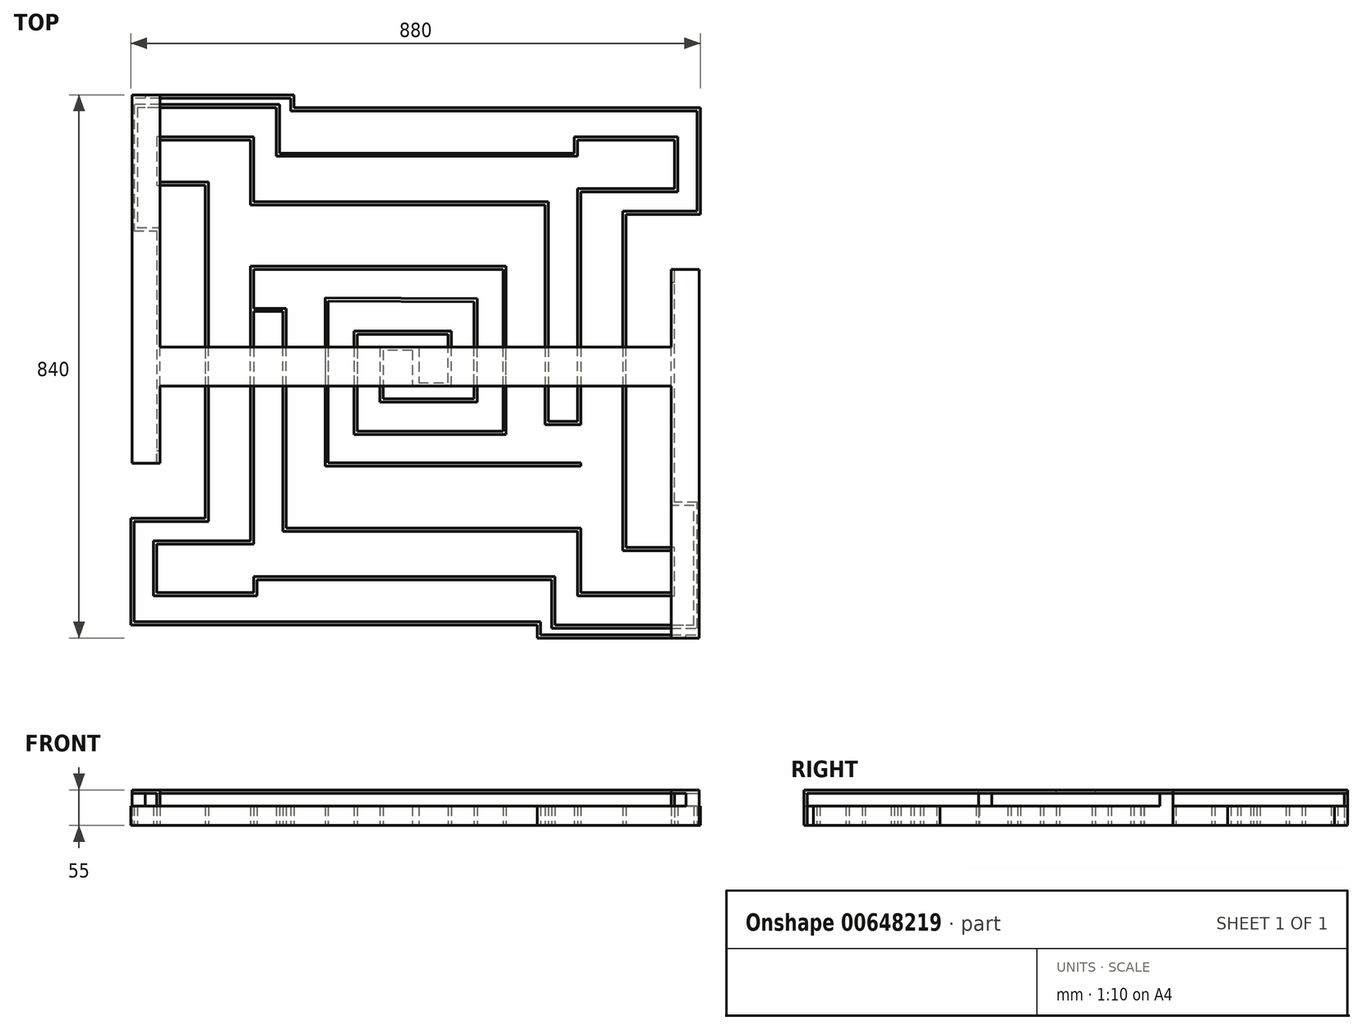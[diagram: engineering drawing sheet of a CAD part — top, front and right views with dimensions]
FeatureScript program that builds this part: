
annotation { "Feature Type Name" : "Feature", "Feature Type Description" : "" }
export const myFeature = defineFeature(function(context is Context, id is Id, definition is map)
    precondition{}
    {
        {
            var Q0;
            Q0=qCreatedBy(makeId("Top.planeOp"),FACE);
            var sketch = newSketch(context, id + "F0", { "sketchPlane" : qUnion([Q0])});
            skLineSegment(sketch, "E0.bottom", {"start": v(150, 150) * mm, "end": v(-150, 150) * mm, "construction": true});
            skLineSegment(sketch, "E0.top", {"start": v(150, -150) * mm, "end": v(-150, -150) * mm, "construction": true});
            skLineSegment(sketch, "E0.left", {"start": v(150, 150) * mm, "end": v(150, -150) * mm, "construction": true});
            skLineSegment(sketch, "E0.right", {"start": v(-150, 150) * mm, "end": v(-150, -150) * mm, "construction": true});
            skPoint(sketch, "E0.middle", {"position": v(0, 0) * mm});
            skPoint(sketch, "E1.0.1.0", {"position": v(0, 325) * mm});
            skLineSegment(sketch, "E1.0.1.1", {"start": v(-150, 475) * mm, "end": v(-150, 175) * mm, "construction": true});
            skLineSegment(sketch, "E1.0.1.2", {"start": v(150, 475) * mm, "end": v(150, 175) * mm, "construction": true});
            skLineSegment(sketch, "E1.0.1.3", {"start": v(150, 175) * mm, "end": v(-150, 175) * mm, "construction": true});
            skLineSegment(sketch, "E1.0.1.4", {"start": v(150, 475) * mm, "end": v(-150, 475) * mm, "construction": true});
            skLineSegment(sketch, "E1.0.2.1", {"start": v(-150, 800) * mm, "end": v(-150, 500) * mm, "construction": true});
            skLineSegment(sketch, "E1.0.2.2", {"start": v(150, 800) * mm, "end": v(150, 500) * mm, "construction": true});
            skLineSegment(sketch, "E1.0.2.3", {"start": v(150, 500) * mm, "end": v(-150, 500) * mm, "construction": true});
            skLineSegment(sketch, "E1.0.2.4", {"start": v(150, 800) * mm, "end": v(-150, 800) * mm, "construction": true});
            skPoint(sketch, "E1.1.0.0", {"position": v(325, 0) * mm});
            skLineSegment(sketch, "E1.1.0.1", {"start": v(175, 150) * mm, "end": v(175, -150) * mm, "construction": true});
            skLineSegment(sketch, "E1.1.0.2", {"start": v(475, 150) * mm, "end": v(475, -150) * mm, "construction": true});
            skLineSegment(sketch, "E1.1.0.3", {"start": v(475, -150) * mm, "end": v(175, -150) * mm, "construction": true});
            skLineSegment(sketch, "E1.1.0.4", {"start": v(475, 150) * mm, "end": v(175, 150) * mm, "construction": true});
            skPoint(sketch, "E1.1.1.0", {"position": v(325, 325) * mm});
            skLineSegment(sketch, "E1.1.1.1", {"start": v(175, 475) * mm, "end": v(175, 175) * mm, "construction": true});
            skLineSegment(sketch, "E1.1.1.2", {"start": v(475, 475) * mm, "end": v(475, 175) * mm, "construction": true});
            skLineSegment(sketch, "E1.1.1.3", {"start": v(475, 175) * mm, "end": v(175, 175) * mm, "construction": true});
            skLineSegment(sketch, "E1.1.1.4", {"start": v(475, 475) * mm, "end": v(175, 475) * mm, "construction": true});
            skPoint(sketch, "E1.1.2.0", {"position": v(325, 650) * mm});
            skLineSegment(sketch, "E1.1.2.1", {"start": v(175, 800) * mm, "end": v(175, 500) * mm, "construction": true});
            skLineSegment(sketch, "E1.1.2.2", {"start": v(475, 800) * mm, "end": v(475, 500) * mm, "construction": true});
            skLineSegment(sketch, "E1.1.2.3", {"start": v(475, 500) * mm, "end": v(175, 500) * mm, "construction": true});
            skLineSegment(sketch, "E1.1.2.4", {"start": v(475, 800) * mm, "end": v(175, 800) * mm, "construction": true});
            skLineSegment(sketch, "E1.2.0.1", {"start": v(500, 150) * mm, "end": v(500, -150) * mm, "construction": true});
            skLineSegment(sketch, "E1.2.0.2", {"start": v(800, 150) * mm, "end": v(800, -150) * mm, "construction": true});
            skLineSegment(sketch, "E1.2.0.3", {"start": v(800, -150) * mm, "end": v(500, -150) * mm, "construction": true});
            skLineSegment(sketch, "E1.2.0.4", {"start": v(800, 150) * mm, "end": v(500, 150) * mm, "construction": true});
            skPoint(sketch, "E1.2.1.0", {"position": v(650, 325) * mm});
            skLineSegment(sketch, "E1.2.1.1", {"start": v(500, 475) * mm, "end": v(500, 175) * mm, "construction": true});
            skLineSegment(sketch, "E1.2.1.2", {"start": v(800, 475) * mm, "end": v(800, 175) * mm, "construction": true});
            skLineSegment(sketch, "E1.2.1.3", {"start": v(800, 175) * mm, "end": v(500, 175) * mm, "construction": true});
            skLineSegment(sketch, "E1.2.1.4", {"start": v(800, 475) * mm, "end": v(500, 475) * mm, "construction": true});
            skLineSegment(sketch, "E1.2.2.1", {"start": v(500, 800) * mm, "end": v(500, 500) * mm, "construction": true});
            skLineSegment(sketch, "E1.2.2.2", {"start": v(800, 800) * mm, "end": v(800, 500) * mm, "construction": true});
            skLineSegment(sketch, "E1.2.2.3", {"start": v(800, 500) * mm, "end": v(500, 500) * mm, "construction": true});
            skLineSegment(sketch, "E1.2.2.4", {"start": v(800, 800) * mm, "end": v(500, 800) * mm, "construction": true});
            skLineSegment(sketch, "E1.direction1", {"start": v(-150, -150) * mm, "end": v(175, -150) * mm, "construction": true});
            skLineSegment(sketch, "E1.direction2", {"start": v(-150, -150) * mm, "end": v(-150, 175) * mm, "construction": true});
            skLineSegment(sketch, "E2", {"start": v(190, 425.96) * mm, "end": v(190, 175.96) * mm});
            skLineSegment(sketch, "E3", {"start": v(190, 175.96) * mm, "end": v(580, 175.96) * mm});
            skLineSegment(sketch, "E4", {"start": v(325, 350) * mm, "end": v(275, 350) * mm});
            skLineSegment(sketch, "E5", {"start": v(275, 350) * mm, "end": v(275, 275) * mm});
            skLineSegment(sketch, "E6", {"start": v(415, 275) * mm, "end": v(415, 425) * mm});
            skLineSegment(sketch, "E7", {"start": v(275, 275) * mm, "end": v(415, 275) * mm});
            skLineSegment(sketch, "E8", {"start": v(415, 425) * mm, "end": v(190, 425.96) * mm});
            skLineSegment(sketch, "E9", {"start": v(325, 350) * mm, "end": v(325, 300) * mm, "construction": true});
            skLineSegment(sketch, "E10", {"start": v(325, 300) * mm, "end": v(375, 300) * mm});
            skLineSegment(sketch, "E11", {"start": v(375, 300) * mm, "end": v(375, 375) * mm});
            skLineSegment(sketch, "E12", {"start": v(375, 375) * mm, "end": v(235, 375) * mm});
            skLineSegment(sketch, "E13", {"start": v(235, 375) * mm, "end": v(235, 225) * mm});
            skLineSegment(sketch, "E14", {"start": v(235, 225) * mm, "end": v(460, 225) * mm});
            skLineSegment(sketch, "E15", {"start": v(460, 225) * mm, "end": v(460, 475) * mm});
            skLineSegment(sketch, "E16", {"start": v(460, 475) * mm, "end": v(70, 475) * mm});
            skLineSegment(sketch, "E17.0", {"start": v(465, 480) * mm, "end": v(70, 480) * mm});
            skLineSegment(sketch, "E17.1", {"start": v(465, 220) * mm, "end": v(465, 480) * mm});
            skLineSegment(sketch, "E17.2", {"start": v(230, 220) * mm, "end": v(465, 220) * mm});
            skLineSegment(sketch, "E17.3", {"start": v(325, 295) * mm, "end": v(380, 295) * mm});
            skLineSegment(sketch, "E17.4", {"start": v(380, 295) * mm, "end": v(380, 380) * mm});
            skLineSegment(sketch, "E17.5", {"start": v(380, 380) * mm, "end": v(230, 380) * mm});
            skLineSegment(sketch, "E17.6", {"start": v(230, 380) * mm, "end": v(230, 220) * mm});
            skLineSegment(sketch, "E18", {"start": v(70, 480) * mm, "end": v(70, 475) * mm});
            skLineSegment(sketch, "E19", {"start": v(325, 300) * mm, "end": v(325, 295) * mm});
            skLineSegment(sketch, "E20.0", {"start": v(185, 170.96) * mm, "end": v(580, 170.96) * mm});
            skLineSegment(sketch, "E20.1", {"start": v(185, 430.98) * mm, "end": v(185, 170.96) * mm});
            skLineSegment(sketch, "E20.2", {"start": v(420, 429.98) * mm, "end": v(185, 430.98) * mm});
            skLineSegment(sketch, "E20.3", {"start": v(325, 355) * mm, "end": v(270, 355) * mm});
            skLineSegment(sketch, "E20.4", {"start": v(270, 355) * mm, "end": v(270, 270) * mm});
            skLineSegment(sketch, "E20.5", {"start": v(270, 270) * mm, "end": v(420, 270) * mm});
            skLineSegment(sketch, "E20.6", {"start": v(420, 270) * mm, "end": v(420, 429.98) * mm});
            skLineSegment(sketch, "E21", {"start": v(580, 175.96) * mm, "end": v(580, 170.96) * mm});
            skLineSegment(sketch, "E22", {"start": v(325, 355) * mm, "end": v(325, 350) * mm});
            skLineSegment(sketch, "E23", {"start": v(125, 75) * mm, "end": v(125, 150) * mm});
            skLineSegment(sketch, "E24", {"start": v(75, 150) * mm, "end": v(75, 50) * mm});
            skLineSegment(sketch, "E25", {"start": v(75, 50) * mm, "end": v(-75, 50) * mm});
            skLineSegment(sketch, "E26", {"start": v(-75, 50) * mm, "end": v(-75, -25) * mm});
            skLineSegment(sketch, "E27", {"start": v(-75, -25) * mm, "end": v(75, -25) * mm});
            skLineSegment(sketch, "E28", {"start": v(75, -25) * mm, "end": v(75, 0) * mm});
            skLineSegment(sketch, "E29", {"start": v(75, 0) * mm, "end": v(150, 0) * mm});
            skLineSegment(sketch, "E30", {"start": v(175, -75) * mm, "end": v(475, -75) * mm});
            skLineSegment(sketch, "E31", {"start": v(125, 75) * mm, "end": v(150, 75) * mm});
            skLineSegment(sketch, "E32", {"start": v(150, -75) * mm, "end": v(-115, -75) * mm});
            skLineSegment(sketch, "E33", {"start": v(-115, -75) * mm, "end": v(-115, 90) * mm});
            skLineSegment(sketch, "E34", {"start": v(-115, 90) * mm, "end": v(0, 90) * mm});
            skLineSegment(sketch, "E35", {"start": v(0, 90) * mm, "end": v(0, 150) * mm});
            skLineSegment(sketch, "E36", {"start": v(175, 0) * mm, "end": v(475, 0) * mm});
            skLineSegment(sketch, "E37", {"start": v(175, 75) * mm, "end": v(475, 75) * mm});
            skLineSegment(sketch, "E38", {"start": v(325, 150) * mm, "end": v(325, -150) * mm, "construction": true});
            skLineSegment(sketch, "E39.0", {"start": v(120, 70) * mm, "end": v(150, 70) * mm});
            skLineSegment(sketch, "E39.1", {"start": v(120, 70) * mm, "end": v(120, 150) * mm});
            skLineSegment(sketch, "E40.0", {"start": v(80, -5) * mm, "end": v(150, -5) * mm});
            skLineSegment(sketch, "E40.1", {"start": v(80, -30) * mm, "end": v(80, -5) * mm});
            skLineSegment(sketch, "E40.2", {"start": v(70, 150) * mm, "end": v(70, 55) * mm});
            skLineSegment(sketch, "E40.3", {"start": v(70, 55) * mm, "end": v(-80, 55) * mm});
            skLineSegment(sketch, "E40.4", {"start": v(-80, 55) * mm, "end": v(-80, -30) * mm});
            skLineSegment(sketch, "E40.5", {"start": v(-80, -30) * mm, "end": v(80, -30) * mm});
            skLineSegment(sketch, "E41.0", {"start": v(5, 85) * mm, "end": v(5, 150) * mm});
            skLineSegment(sketch, "E41.1", {"start": v(-110, 85) * mm, "end": v(5, 85) * mm});
            skLineSegment(sketch, "E41.2", {"start": v(-110, -70) * mm, "end": v(-110, 85) * mm});
            skLineSegment(sketch, "E41.3", {"start": v(150, -70) * mm, "end": v(-110, -70) * mm});
            skLineSegment(sketch, "E42.0", {"start": v(175, 70) * mm, "end": v(475, 70) * mm});
            skLineSegment(sketch, "E43.0", {"start": v(175, -5) * mm, "end": v(475, -5) * mm});
            skLineSegment(sketch, "E44.0", {"start": v(175, -70) * mm, "end": v(475, -70) * mm});
            skLineSegment(sketch, "E45", {"start": v(0, 175) * mm, "end": v(0, 475) * mm});
            skLineSegment(sketch, "E46", {"start": v(-75, 175) * mm, "end": v(-75, 475) * mm});
            skLineSegment(sketch, "E47", {"start": v(175, 75) * mm, "end": v(150, 75) * mm});
            skLineSegment(sketch, "E48", {"start": v(175, 70) * mm, "end": v(150, 70) * mm});
            skLineSegment(sketch, "E49", {"start": v(175, 0) * mm, "end": v(150, 0) * mm});
            skLineSegment(sketch, "E50", {"start": v(175, -5) * mm, "end": v(150, -5) * mm});
            skLineSegment(sketch, "E51", {"start": v(175, -70) * mm, "end": v(150, -70) * mm});
            skLineSegment(sketch, "E52", {"start": v(175, -75) * mm, "end": v(150, -75) * mm});
            skLineSegment(sketch, "E53.0", {"start": v(5, 175) * mm, "end": v(5, 475) * mm});
            skLineSegment(sketch, "E54", {"start": v(5, 150) * mm, "end": v(5, 175) * mm});
            skLineSegment(sketch, "E55", {"start": v(70, 150) * mm, "end": v(70, 175) * mm});
            skLineSegment(sketch, "E56", {"start": v(75, 150) * mm, "end": v(75, 175) * mm});
            skLineSegment(sketch, "E57", {"start": v(120, 150) * mm, "end": v(120, 175) * mm});
            skLineSegment(sketch, "E58", {"start": v(125, 150) * mm, "end": v(125, 175) * mm});
            skLineSegment(sketch, "E59.MirrorCS", {"start": v(475, -75) * mm, "end": v(500, -75) * mm});
            skLineSegment(sketch, "E60.MirrorCS", {"start": v(475, -70) * mm, "end": v(500, -70) * mm});
            skLineSegment(sketch, "E61.MirrorCS", {"start": v(475, 70) * mm, "end": v(500, 70) * mm});
            skLineSegment(sketch, "E62.MirrorCS", {"start": v(475, -5) * mm, "end": v(500, -5) * mm});
            skLineSegment(sketch, "E63.MirrorCS", {"start": v(475, 75) * mm, "end": v(500, 75) * mm});
            skLineSegment(sketch, "E64.MirrorCS", {"start": v(475, 0) * mm, "end": v(500, 0) * mm});
            skLineSegment(sketch, "E65", {"start": v(500, 70) * mm, "end": v(575, 70) * mm});
            skLineSegment(sketch, "E66", {"start": v(575, 70) * mm, "end": v(575, -30) * mm});
            skLineSegment(sketch, "E67", {"start": v(575, -30) * mm, "end": v(725, -30) * mm});
            skLineSegment(sketch, "E68", {"start": v(725, -30) * mm, "end": v(725, 45) * mm});
            skLineSegment(sketch, "E69", {"start": v(725, 45) * mm, "end": v(650, 45) * mm});
            skLineSegment(sketch, "E70", {"start": v(650, 45) * mm, "end": v(650, 150) * mm});
            skLineSegment(sketch, "E71", {"start": v(500, -5) * mm, "end": v(535, -5) * mm});
            skLineSegment(sketch, "E72", {"start": v(535, -5) * mm, "end": v(535, -80) * mm});
            skLineSegment(sketch, "E73", {"start": v(535, -80) * mm, "end": v(760, -80) * mm});
            skLineSegment(sketch, "E74", {"start": v(760, -80) * mm, "end": v(760, 115) * mm});
            skLineSegment(sketch, "E75", {"start": v(760, 115) * mm, "end": v(725, 115) * mm});
            skLineSegment(sketch, "E76", {"start": v(725, 115) * mm, "end": v(725, 150) * mm});
            skLineSegment(sketch, "E77", {"start": v(500, -75) * mm, "end": v(513.03, -75) * mm});
            skLineSegment(sketch, "E78", {"start": v(513.03, -75) * mm, "end": v(513.03, -95) * mm});
            skLineSegment(sketch, "E79", {"start": v(513.03, -95) * mm, "end": v(763.03, -95) * mm});
            skLineSegment(sketch, "E80.0", {"start": v(518.03, -90) * mm, "end": v(763.03, -90) * mm});
            skLineSegment(sketch, "E80.1", {"start": v(518.03, -70) * mm, "end": v(518.03, -90) * mm});
            skLineSegment(sketch, "E80.2", {"start": v(500, -70) * mm, "end": v(518.03, -70) * mm});
            skLineSegment(sketch, "E81.0", {"start": v(645, 40) * mm, "end": v(645, 150) * mm});
            skLineSegment(sketch, "E81.1", {"start": v(720, 40) * mm, "end": v(645, 40) * mm});
            skLineSegment(sketch, "E81.2", {"start": v(500, 75) * mm, "end": v(580, 75) * mm});
            skLineSegment(sketch, "E81.3", {"start": v(580, 75) * mm, "end": v(580, -25) * mm});
            skLineSegment(sketch, "E81.4", {"start": v(580, -25) * mm, "end": v(720, -25) * mm});
            skLineSegment(sketch, "E81.5", {"start": v(720, -25) * mm, "end": v(720, 40) * mm});
            skLineSegment(sketch, "E82.0", {"start": v(720, 110) * mm, "end": v(720, 150) * mm});
            skLineSegment(sketch, "E82.1", {"start": v(755, 110) * mm, "end": v(720, 110) * mm});
            skLineSegment(sketch, "E82.2", {"start": v(500, 0) * mm, "end": v(540, 0) * mm});
            skLineSegment(sketch, "E82.3", {"start": v(540, 0) * mm, "end": v(540, -75) * mm});
            skLineSegment(sketch, "E82.4", {"start": v(540, -75) * mm, "end": v(755, -75) * mm});
            skLineSegment(sketch, "E82.5", {"start": v(755, -75) * mm, "end": v(755, 110) * mm});
            skLineSegment(sketch, "E83", {"start": v(650, 175) * mm, "end": v(650, 475) * mm});
            skLineSegment(sketch, "E84", {"start": v(725, 175) * mm, "end": v(725, 475) * mm});
            skLineSegment(sketch, "E85.0", {"start": v(645, 175) * mm, "end": v(645, 475) * mm});
            skLineSegment(sketch, "E86.0", {"start": v(720, 175) * mm, "end": v(720, 475) * mm});
            skLineSegment(sketch, "E87", {"start": v(650, 150) * mm, "end": v(650, 175) * mm});
            skLineSegment(sketch, "E88", {"start": v(645, 150) * mm, "end": v(645, 175) * mm});
            skLineSegment(sketch, "E89", {"start": v(725, 150) * mm, "end": v(725, 175) * mm});
            skLineSegment(sketch, "E90", {"start": v(720, 150) * mm, "end": v(720, 175) * mm});
            skLineSegment(sketch, "E91", {"start": v(525, 475) * mm, "end": v(525, 235) * mm});
            skLineSegment(sketch, "E92", {"start": v(575, 475) * mm, "end": v(575, 240) * mm});
            skLineSegment(sketch, "E93", {"start": v(150, 325) * mm, "end": v(-150, 325) * mm, "construction": true});
            skLineSegment(sketch, "E94.0", {"start": v(580, 475) * mm, "end": v(580, 235) * mm});
            skLineSegment(sketch, "E95.0", {"start": v(530, 475) * mm, "end": v(530, 240) * mm});
            skLineSegment(sketch, "E96", {"start": v(763.03, -90) * mm, "end": v(763.03, -95) * mm});
            skLineSegment(sketch, "E97.MirrorCS", {"start": v(-113.03, 740) * mm, "end": v(-113.03, 745) * mm});
            skLineSegment(sketch, "E98.MirrorCS", {"start": v(150, 725) * mm, "end": v(136.97, 725) * mm});
            skLineSegment(sketch, "E99.MirrorCS", {"start": v(150, 720) * mm, "end": v(131.97, 720) * mm});
            skLineSegment(sketch, "E100.MirrorCS", {"start": v(-105, 725) * mm, "end": v(-105, 540) * mm});
            skLineSegment(sketch, "E101.MirrorCS", {"start": v(150, 580) * mm, "end": v(75, 580) * mm});
            skLineSegment(sketch, "E102.MirrorCS", {"start": v(136.97, 745) * mm, "end": v(-113.03, 745) * mm});
            skLineSegment(sketch, "E103.MirrorCS", {"start": v(-70, 675) * mm, "end": v(-70, 610) * mm});
            skLineSegment(sketch, "E104.MirrorCS", {"start": v(-110, 730) * mm, "end": v(-110, 535) * mm});
            skLineSegment(sketch, "E105.MirrorCS", {"start": v(-70, 540) * mm, "end": v(-70, 500) * mm});
            skLineSegment(sketch, "E106.MirrorCS", {"start": v(-75, 605) * mm, "end": v(0, 605) * mm});
            skLineSegment(sketch, "E107.MirrorCS", {"start": v(70, 575) * mm, "end": v(70, 675) * mm});
            skLineSegment(sketch, "E108.MirrorCS", {"start": v(-75, 535) * mm, "end": v(-75, 500) * mm});
            skLineSegment(sketch, "E109.MirrorCS", {"start": v(-105, 540) * mm, "end": v(-70, 540) * mm});
            skLineSegment(sketch, "E110.MirrorCS", {"start": v(-70, 610) * mm, "end": v(5, 610) * mm});
            skLineSegment(sketch, "E111.MirrorCS", {"start": v(5, 610) * mm, "end": v(5, 500) * mm});
            skLineSegment(sketch, "E112.MirrorCS", {"start": v(70, 675) * mm, "end": v(-70, 675) * mm});
            skLineSegment(sketch, "E113.MirrorCS", {"start": v(115, 730) * mm, "end": v(-110, 730) * mm});
            skLineSegment(sketch, "E114.MirrorCS", {"start": v(131.97, 740) * mm, "end": v(-113.03, 740) * mm});
            skLineSegment(sketch, "E115.MirrorCS", {"start": v(150, 655) * mm, "end": v(115, 655) * mm});
            skLineSegment(sketch, "E116.MirrorCS", {"start": v(110, 650) * mm, "end": v(110, 725) * mm});
            skLineSegment(sketch, "E117.MirrorCS", {"start": v(150, 575) * mm, "end": v(70, 575) * mm});
            skLineSegment(sketch, "E118.MirrorCS", {"start": v(-110, 535) * mm, "end": v(-75, 535) * mm});
            skLineSegment(sketch, "E119.MirrorCS", {"start": v(75, 580) * mm, "end": v(75, 680) * mm});
            skLineSegment(sketch, "E120.MirrorCS", {"start": v(136.97, 725) * mm, "end": v(136.97, 745) * mm});
            skLineSegment(sketch, "E121.MirrorCS", {"start": v(115, 655) * mm, "end": v(115, 730) * mm});
            skLineSegment(sketch, "E122.MirrorCS", {"start": v(131.97, 720) * mm, "end": v(131.97, 740) * mm});
            skLineSegment(sketch, "E123.MirrorCS", {"start": v(110, 725) * mm, "end": v(-105, 725) * mm});
            skLineSegment(sketch, "E124.MirrorCS", {"start": v(-75, 680) * mm, "end": v(-75, 605) * mm});
            skLineSegment(sketch, "E125.MirrorCS", {"start": v(0, 605) * mm, "end": v(0, 500) * mm});
            skLineSegment(sketch, "E126.MirrorCS", {"start": v(150, 650) * mm, "end": v(110, 650) * mm});
            skLineSegment(sketch, "E127.MirrorCS", {"start": v(75, 680) * mm, "end": v(-75, 680) * mm});
            skPoint(sketch, "E128.2.2.0", {"position": v(650, 650) * mm});
            skLineSegment(sketch, "E129.MirrorCS", {"start": v(570, 680) * mm, "end": v(570, 655) * mm});
            skLineSegment(sketch, "E130.MirrorCS", {"start": v(575, 675) * mm, "end": v(575, 650) * mm});
            skLineSegment(sketch, "E131.MirrorCS", {"start": v(525, 575) * mm, "end": v(500, 575) * mm});
            skLineSegment(sketch, "E132.MirrorCS", {"start": v(570, 655) * mm, "end": v(500, 655) * mm});
            skLineSegment(sketch, "E133.MirrorCS", {"start": v(530, 580) * mm, "end": v(500, 580) * mm});
            skLineSegment(sketch, "E134.MirrorCS", {"start": v(580, 595) * mm, "end": v(730, 595) * mm});
            skLineSegment(sketch, "E135.MirrorCS", {"start": v(730, 595) * mm, "end": v(730, 680) * mm});
            skLineSegment(sketch, "E136.MirrorCS", {"start": v(650, 560) * mm, "end": v(650, 500) * mm});
            skLineSegment(sketch, "E137.MirrorCS", {"start": v(580, 500) * mm, "end": v(580, 595) * mm});
            skLineSegment(sketch, "E138.MirrorCS", {"start": v(645, 565) * mm, "end": v(645, 500) * mm});
            skLineSegment(sketch, "E139.MirrorCS", {"start": v(760, 565) * mm, "end": v(645, 565) * mm});
            skLineSegment(sketch, "E140.MirrorCS", {"start": v(575, 600) * mm, "end": v(725, 600) * mm});
            skLineSegment(sketch, "E141.MirrorCS", {"start": v(575, 650) * mm, "end": v(500, 650) * mm});
            skLineSegment(sketch, "E142.MirrorCS", {"start": v(730, 680) * mm, "end": v(570, 680) * mm});
            skLineSegment(sketch, "E143.MirrorCS", {"start": v(500, 720) * mm, "end": v(760, 720) * mm});
            skLineSegment(sketch, "E144.MirrorCS", {"start": v(765, 560) * mm, "end": v(650, 560) * mm});
            skLineSegment(sketch, "E145.MirrorCS", {"start": v(575, 500) * mm, "end": v(575, 600) * mm});
            skLineSegment(sketch, "E146.MirrorCS", {"start": v(525, 575) * mm, "end": v(525, 500) * mm});
            skLineSegment(sketch, "E147.MirrorCS", {"start": v(760, 720) * mm, "end": v(760, 565) * mm});
            skLineSegment(sketch, "E148.MirrorCS", {"start": v(765, 725) * mm, "end": v(765, 560) * mm});
            skLineSegment(sketch, "E149.MirrorCS", {"start": v(725, 675) * mm, "end": v(575, 675) * mm});
            skLineSegment(sketch, "E150.MirrorCS", {"start": v(500, 725) * mm, "end": v(765, 725) * mm});
            skLineSegment(sketch, "E151.MirrorCS", {"start": v(725, 600) * mm, "end": v(725, 675) * mm});
            skLineSegment(sketch, "E152.MirrorCS", {"start": v(530, 580) * mm, "end": v(530, 500) * mm});
            skLineSegment(sketch, "E153.MirrorCS", {"start": v(175, 725) * mm, "end": v(475, 725) * mm});
            skLineSegment(sketch, "E154.MirrorCS", {"start": v(175, 720) * mm, "end": v(475, 720) * mm});
            skLineSegment(sketch, "E155.MirrorCS", {"start": v(175, 655) * mm, "end": v(475, 655) * mm});
            skLineSegment(sketch, "E156.MirrorCS", {"start": v(175, 650) * mm, "end": v(475, 650) * mm});
            skLineSegment(sketch, "E157.MirrorCS", {"start": v(175, 575) * mm, "end": v(475, 575) * mm});
            skLineSegment(sketch, "E158.MirrorCS", {"start": v(175, 580) * mm, "end": v(475, 580) * mm});
            skLineSegment(sketch, "E159", {"start": v(150, 725) * mm, "end": v(175, 725) * mm});
            skLineSegment(sketch, "E160", {"start": v(150, 720) * mm, "end": v(175, 720) * mm});
            skLineSegment(sketch, "E161", {"start": v(150, 655) * mm, "end": v(175, 655) * mm});
            skLineSegment(sketch, "E162", {"start": v(150, 650) * mm, "end": v(175, 650) * mm});
            skLineSegment(sketch, "E163", {"start": v(150, 580) * mm, "end": v(175, 580) * mm});
            skLineSegment(sketch, "E164", {"start": v(150, 575) * mm, "end": v(175, 575) * mm});
            skLineSegment(sketch, "E165", {"start": v(475, 725) * mm, "end": v(500, 725) * mm});
            skLineSegment(sketch, "E166", {"start": v(475, 720) * mm, "end": v(500, 720) * mm});
            skLineSegment(sketch, "E167", {"start": v(475, 655) * mm, "end": v(500, 655) * mm});
            skLineSegment(sketch, "E168", {"start": v(475, 650) * mm, "end": v(500, 650) * mm});
            skLineSegment(sketch, "E169", {"start": v(475, 580) * mm, "end": v(500, 580) * mm});
            skLineSegment(sketch, "E170", {"start": v(475, 575) * mm, "end": v(500, 575) * mm});
            skLineSegment(sketch, "E171", {"start": v(530, 500) * mm, "end": v(530, 475) * mm});
            skLineSegment(sketch, "E172", {"start": v(525, 500) * mm, "end": v(525, 475) * mm});
            skLineSegment(sketch, "E173", {"start": v(580, 500) * mm, "end": v(580, 475) * mm});
            skLineSegment(sketch, "E174", {"start": v(575, 500) * mm, "end": v(575, 475) * mm});
            skLineSegment(sketch, "E175", {"start": v(650, 500) * mm, "end": v(650, 475) * mm});
            skLineSegment(sketch, "E176", {"start": v(645, 500) * mm, "end": v(645, 475) * mm});
            skLineSegment(sketch, "E177", {"start": v(5, 475) * mm, "end": v(5, 500) * mm});
            skLineSegment(sketch, "E178", {"start": v(0, 475) * mm, "end": v(0, 500) * mm});
            skLineSegment(sketch, "E179.0", {"start": v(-70, 175) * mm, "end": v(-70, 475) * mm});
            skLineSegment(sketch, "E180", {"start": v(-75, 500) * mm, "end": v(-75, 475) * mm});
            skLineSegment(sketch, "E181", {"start": v(-70, 500) * mm, "end": v(-70, 475) * mm});
            skLineSegment(sketch, "E182", {"start": v(530, 240) * mm, "end": v(575, 240) * mm});
            skLineSegment(sketch, "E183", {"start": v(525, 235) * mm, "end": v(580, 235) * mm});
            skLineSegment(sketch, "E184", {"start": v(70, 175) * mm, "end": v(70, 415) * mm});
            skLineSegment(sketch, "E185", {"start": v(75, 175) * mm, "end": v(75, 410) * mm});
            skLineSegment(sketch, "E186", {"start": v(125, 175) * mm, "end": v(125, 415) * mm});
            skLineSegment(sketch, "E187", {"start": v(120, 175) * mm, "end": v(120, 410) * mm});
            skLineSegment(sketch, "E188", {"start": v(70, 415) * mm, "end": v(125, 415) * mm});
            skLineSegment(sketch, "E189", {"start": v(75, 410) * mm, "end": v(120, 410) * mm});
            skLineSegment(sketch, "E190", {"start": v(0, 175) * mm, "end": v(0, 150) * mm});
            skLineSegment(sketch, "E191", {"start": v(-70, 175) * mm, "end": v(-75, 175) * mm});
            skLineSegment(sketch, "E192", {"start": v(725, 475) * mm, "end": v(720, 475) * mm});
            skLineSegment(sketch, "E193", {"start": v(70, 475) * mm, "end": v(70, 415) * mm});
            skLineSegment(sketch, "E194.0", {"start": v(75, 475) * mm, "end": v(75, 415) * mm});
            skLineSegment(sketch, "E195", {"start": v(580, 175.96) * mm, "end": v(580, 235) * mm});
            skLineSegment(sketch, "E196.0", {"start": v(575, 175.96) * mm, "end": v(575, 235) * mm});
            skLineSegment(sketch, "E197", {"start": v(325, 355) * mm, "end": v(325, 295) * mm});
            skLineSegment(sketch, "E198.0", {"start": v(320, 355) * mm, "end": v(320, 295) * mm});
            skLineSegment(sketch, "E199.0", {"start": v(330, 355) * mm, "end": v(330, 295) * mm});
            skLineSegment(sketch, "E200", {"start": v(325, 355) * mm, "end": v(330, 355) * mm});
            skLineSegment(sketch, "E201", {"start": v(320, 295) * mm, "end": v(325, 295) * mm});
            skSolve(sketch);
        }
        {
            var Q0;
            Q0=makeQuery(id+"F0.imprint","IMPRINT",FACE,{"disambiguationData":[TD([[makeQuery(id+"F0.imprint","IMPRINT",EDGE,{"derivedFrom":sQuery(id+"F0.wireOp",EDGE,"E30")}),1.0]])]});
            var Q1;
            Q1=makeQuery(id+"F0.imprint","IMPRINT",FACE,{"disambiguationData":[TD([[makeQuery(id+"F0.imprint","IMPRINT",EDGE,{"derivedFrom":sQuery(id+"F0.wireOp",EDGE,"E23")}),1.0]])]});
            var Q2;
            Q2=makeQuery(id+"F0.imprint","IMPRINT",FACE,{"disambiguationData":[TD([[makeQuery(id+"F0.imprint","IMPRINT",EDGE,{"derivedFrom":sQuery(id+"F0.wireOp",EDGE,"E10")}),-1.0]])]});
            var Q3;
            Q3=makeQuery(id+"F0.imprint","IMPRINT",FACE,{"disambiguationData":[TD([[makeQuery(id+"F0.imprint","IMPRINT",EDGE,{"derivedFrom":sQuery(id+"F0.wireOp",EDGE,"E2")}),-1.0]])]});
            var Q4;
            {var subQ0=sQuery(id+"F0.wireOp",EDGE,"E193");Q4=makeQuery(id+"F0.imprint","IMPRINT",FACE,{"disambiguationData":[TD([[makeQuery(id+"F0.imprint","IMPRINT",EDGE,{"derivedFrom":subQ0}),1.0]])]});}
            var Q5;
            {var subQ0=sQuery(id+"F0.wireOp",EDGE,"E195");Q5=makeQuery(id+"F0.imprint","IMPRINT",FACE,{"disambiguationData":[TD([[makeQuery(id+"F0.imprint","IMPRINT",EDGE,{"derivedFrom":subQ0}),1.0]])]});}
            var Q6;
            {var subQ0=sQuery(id+"F0.wireOp",EDGE,"E201");Q6=makeQuery(id+"F0.imprint","IMPRINT",FACE,{"disambiguationData":[TD([[makeQuery(id+"F0.imprint","IMPRINT",EDGE,{"derivedFrom":subQ0}),1.0]])]});}
            var Q7;
            {var subQ4=sQuery(id+"F0.wireOp",EDGE,"E11");Q7=makeQuery(id+"F0.imprint","IMPRINT",FACE,{"disambiguationData":[TD([[makeQuery(id+"F0.imprint","IMPRINT",EDGE,{"derivedFrom":subQ4}),-1.0]])]});}
            var Q8;
            {var subQ4=sQuery(id+"F0.wireOp",EDGE,"E200");Q8=makeQuery(id+"F0.imprint","IMPRINT",FACE,{"disambiguationData":[TD([[makeQuery(id+"F0.imprint","IMPRINT",EDGE,{"derivedFrom":subQ4}),-1.0]])]});}
            var Q9;
            {var subQ0=sQuery(id+"F0.wireOp",EDGE,"E197");var subQ1=sQuery(id+"F0.wireOp",EDGE,"E4");var subQ2=makeQuery(id+"F0.imprint","INTERSECT",VERTEX,{"derivedFrom":[subQ1,subQ0]});Q9=makeQuery(id+"F0.imprint","IMPRINT",FACE,{"disambiguationData":[TD([[makeQuery(id+"F0.imprint","IMPRINT",EDGE,{"disambiguationData":[TD([[subQ2,-1.0]])],"derivedFrom":subQ1}),-1.0]])]});}
            extrude(context, id + "F1", {"entities" : qUnion([Q0, Q1, Q2, Q3, Q4, Q5, Q6, Q7, Q8, Q9]), "depth" : 30 * mm, "offsetDistance" : 25 * mm});
        }
        {
            var Q0;
            Q0=makeQuery(id+"F1.opExtrude","CAP_FACE",FACE,{"disambiguationData":[OSD([sQuery(id+"F0.wireOp",EDGE,"E2"),sQuery(id+"F0.wireOp",EDGE,"E3"),sQuery(id+"F0.wireOp",EDGE,"E4"),sQuery(id+"F0.wireOp",EDGE,"E5"),sQuery(id+"F0.wireOp",EDGE,"E6"),sQuery(id+"F0.wireOp",EDGE,"E7"),sQuery(id+"F0.wireOp",EDGE,"E8"),sQuery(id+"F0.wireOp",EDGE,"E10"),sQuery(id+"F0.wireOp",EDGE,"E11"),sQuery(id+"F0.wireOp",EDGE,"E12"),sQuery(id+"F0.wireOp",EDGE,"E13"),sQuery(id+"F0.wireOp",EDGE,"E14"),sQuery(id+"F0.wireOp",EDGE,"E15"),sQuery(id+"F0.wireOp",EDGE,"E16"),sQuery(id+"F0.wireOp",EDGE,"E17.0"),sQuery(id+"F0.wireOp",EDGE,"E17.1"),sQuery(id+"F0.wireOp",EDGE,"E17.2"),sQuery(id+"F0.wireOp",EDGE,"E17.3"),sQuery(id+"F0.wireOp",EDGE,"E17.4"),sQuery(id+"F0.wireOp",EDGE,"E17.5"),sQuery(id+"F0.wireOp",EDGE,"E17.6"),sQuery(id+"F0.wireOp",EDGE,"E18"),sQuery(id+"F0.wireOp",EDGE,"E20.0"),sQuery(id+"F0.wireOp",EDGE,"E20.1"),sQuery(id+"F0.wireOp",EDGE,"E20.2"),sQuery(id+"F0.wireOp",EDGE,"E20.3"),sQuery(id+"F0.wireOp",EDGE,"E20.4"),sQuery(id+"F0.wireOp",EDGE,"E20.5"),sQuery(id+"F0.wireOp",EDGE,"E20.6"),sQuery(id+"F0.wireOp",EDGE,"E21"),sQuery(id+"F0.wireOp",EDGE,"E23"),sQuery(id+"F0.wireOp",EDGE,"E24"),sQuery(id+"F0.wireOp",EDGE,"E25"),sQuery(id+"F0.wireOp",EDGE,"E26"),sQuery(id+"F0.wireOp",EDGE,"E27"),sQuery(id+"F0.wireOp",EDGE,"E28"),sQuery(id+"F0.wireOp",EDGE,"E29"),sQuery(id+"F0.wireOp",EDGE,"E30"),sQuery(id+"F0.wireOp",EDGE,"E31"),sQuery(id+"F0.wireOp",EDGE,"E32"),sQuery(id+"F0.wireOp",EDGE,"E33"),sQuery(id+"F0.wireOp",EDGE,"E34"),sQuery(id+"F0.wireOp",EDGE,"E35"),sQuery(id+"F0.wireOp",EDGE,"E39.0"),sQuery(id+"F0.wireOp",EDGE,"E39.1"),sQuery(id+"F0.wireOp",EDGE,"E40.0"),sQuery(id+"F0.wireOp",EDGE,"E40.1"),sQuery(id+"F0.wireOp",EDGE,"E40.2"),sQuery(id+"F0.wireOp",EDGE,"E40.3"),sQuery(id+"F0.wireOp",EDGE,"E40.4"),sQuery(id+"F0.wireOp",EDGE,"E40.5"),sQuery(id+"F0.wireOp",EDGE,"E41.0"),sQuery(id+"F0.wireOp",EDGE,"E41.1"),sQuery(id+"F0.wireOp",EDGE,"E41.2"),sQuery(id+"F0.wireOp",EDGE,"E41.3"),sQuery(id+"F0.wireOp",EDGE,"E42.0"),sQuery(id+"F0.wireOp",EDGE,"E43.0"),sQuery(id+"F0.wireOp",EDGE,"E44.0"),sQuery(id+"F0.wireOp",EDGE,"E36"),sQuery(id+"F0.wireOp",EDGE,"E37"),sQuery(id+"F0.wireOp",EDGE,"E45"),sQuery(id+"F0.wireOp",EDGE,"E46"),sQuery(id+"F0.wireOp",EDGE,"E47"),sQuery(id+"F0.wireOp",EDGE,"E48"),sQuery(id+"F0.wireOp",EDGE,"E49"),sQuery(id+"F0.wireOp",EDGE,"E50"),sQuery(id+"F0.wireOp",EDGE,"E51"),sQuery(id+"F0.wireOp",EDGE,"E52"),sQuery(id+"F0.wireOp",EDGE,"E53.0"),sQuery(id+"F0.wireOp",EDGE,"E54"),sQuery(id+"F0.wireOp",EDGE,"E55"),sQuery(id+"F0.wireOp",EDGE,"E56"),sQuery(id+"F0.wireOp",EDGE,"E57"),sQuery(id+"F0.wireOp",EDGE,"E58"),sQuery(id+"F0.wireOp",EDGE,"E59.MirrorCS"),sQuery(id+"F0.wireOp",EDGE,"E60.MirrorCS"),sQuery(id+"F0.wireOp",EDGE,"E61.MirrorCS"),sQuery(id+"F0.wireOp",EDGE,"E62.MirrorCS"),sQuery(id+"F0.wireOp",EDGE,"E63.MirrorCS"),sQuery(id+"F0.wireOp",EDGE,"E64.MirrorCS"),sQuery(id+"F0.wireOp",EDGE,"E65"),sQuery(id+"F0.wireOp",EDGE,"E66"),sQuery(id+"F0.wireOp",EDGE,"E67"),sQuery(id+"F0.wireOp",EDGE,"E68"),sQuery(id+"F0.wireOp",EDGE,"E69"),sQuery(id+"F0.wireOp",EDGE,"E70"),sQuery(id+"F0.wireOp",EDGE,"E71"),sQuery(id+"F0.wireOp",EDGE,"E72"),sQuery(id+"F0.wireOp",EDGE,"E73"),sQuery(id+"F0.wireOp",EDGE,"E74"),sQuery(id+"F0.wireOp",EDGE,"E75"),sQuery(id+"F0.wireOp",EDGE,"E76"),sQuery(id+"F0.wireOp",EDGE,"E77"),sQuery(id+"F0.wireOp",EDGE,"E78"),sQuery(id+"F0.wireOp",EDGE,"E79"),sQuery(id+"F0.wireOp",EDGE,"E80.0"),sQuery(id+"F0.wireOp",EDGE,"E80.1"),sQuery(id+"F0.wireOp",EDGE,"E80.2"),sQuery(id+"F0.wireOp",EDGE,"E81.0"),sQuery(id+"F0.wireOp",EDGE,"E81.1"),sQuery(id+"F0.wireOp",EDGE,"E81.2"),sQuery(id+"F0.wireOp",EDGE,"E81.3"),sQuery(id+"F0.wireOp",EDGE,"E81.4"),sQuery(id+"F0.wireOp",EDGE,"E81.5"),sQuery(id+"F0.wireOp",EDGE,"E82.0"),sQuery(id+"F0.wireOp",EDGE,"E82.1"),sQuery(id+"F0.wireOp",EDGE,"E82.2"),sQuery(id+"F0.wireOp",EDGE,"E82.3"),sQuery(id+"F0.wireOp",EDGE,"E82.4"),sQuery(id+"F0.wireOp",EDGE,"E82.5"),sQuery(id+"F0.wireOp",EDGE,"E83"),sQuery(id+"F0.wireOp",EDGE,"E84"),sQuery(id+"F0.wireOp",EDGE,"E85.0"),sQuery(id+"F0.wireOp",EDGE,"E86.0"),sQuery(id+"F0.wireOp",EDGE,"E87"),sQuery(id+"F0.wireOp",EDGE,"E88"),sQuery(id+"F0.wireOp",EDGE,"E89"),sQuery(id+"F0.wireOp",EDGE,"E90"),sQuery(id+"F0.wireOp",EDGE,"E91"),sQuery(id+"F0.wireOp",EDGE,"E92"),sQuery(id+"F0.wireOp",EDGE,"E94.0"),sQuery(id+"F0.wireOp",EDGE,"E95.0"),sQuery(id+"F0.wireOp",EDGE,"E96"),sQuery(id+"F0.wireOp",EDGE,"E97.MirrorCS"),sQuery(id+"F0.wireOp",EDGE,"E98.MirrorCS"),sQuery(id+"F0.wireOp",EDGE,"E99.MirrorCS"),sQuery(id+"F0.wireOp",EDGE,"E100.MirrorCS"),sQuery(id+"F0.wireOp",EDGE,"E101.MirrorCS"),sQuery(id+"F0.wireOp",EDGE,"E102.MirrorCS"),sQuery(id+"F0.wireOp",EDGE,"E103.MirrorCS"),sQuery(id+"F0.wireOp",EDGE,"E104.MirrorCS"),sQuery(id+"F0.wireOp",EDGE,"E105.MirrorCS"),sQuery(id+"F0.wireOp",EDGE,"E106.MirrorCS"),sQuery(id+"F0.wireOp",EDGE,"E107.MirrorCS"),sQuery(id+"F0.wireOp",EDGE,"E108.MirrorCS"),sQuery(id+"F0.wireOp",EDGE,"E109.MirrorCS"),sQuery(id+"F0.wireOp",EDGE,"E110.MirrorCS"),sQuery(id+"F0.wireOp",EDGE,"E111.MirrorCS"),sQuery(id+"F0.wireOp",EDGE,"E112.MirrorCS"),sQuery(id+"F0.wireOp",EDGE,"E113.MirrorCS"),sQuery(id+"F0.wireOp",EDGE,"E114.MirrorCS"),sQuery(id+"F0.wireOp",EDGE,"E115.MirrorCS"),sQuery(id+"F0.wireOp",EDGE,"E116.MirrorCS"),sQuery(id+"F0.wireOp",EDGE,"E117.MirrorCS"),sQuery(id+"F0.wireOp",EDGE,"E118.MirrorCS"),sQuery(id+"F0.wireOp",EDGE,"E119.MirrorCS"),sQuery(id+"F0.wireOp",EDGE,"E120.MirrorCS"),sQuery(id+"F0.wireOp",EDGE,"E121.MirrorCS"),sQuery(id+"F0.wireOp",EDGE,"E122.MirrorCS"),sQuery(id+"F0.wireOp",EDGE,"E123.MirrorCS"),sQuery(id+"F0.wireOp",EDGE,"E124.MirrorCS"),sQuery(id+"F0.wireOp",EDGE,"E125.MirrorCS"),sQuery(id+"F0.wireOp",EDGE,"E126.MirrorCS"),sQuery(id+"F0.wireOp",EDGE,"E127.MirrorCS"),sQuery(id+"F0.wireOp",EDGE,"E129.MirrorCS"),sQuery(id+"F0.wireOp",EDGE,"E130.MirrorCS"),sQuery(id+"F0.wireOp",EDGE,"E131.MirrorCS"),sQuery(id+"F0.wireOp",EDGE,"E132.MirrorCS"),sQuery(id+"F0.wireOp",EDGE,"E133.MirrorCS"),sQuery(id+"F0.wireOp",EDGE,"E134.MirrorCS"),sQuery(id+"F0.wireOp",EDGE,"E135.MirrorCS"),sQuery(id+"F0.wireOp",EDGE,"E136.MirrorCS"),sQuery(id+"F0.wireOp",EDGE,"E137.MirrorCS"),sQuery(id+"F0.wireOp",EDGE,"E138.MirrorCS"),sQuery(id+"F0.wireOp",EDGE,"E139.MirrorCS"),sQuery(id+"F0.wireOp",EDGE,"E140.MirrorCS"),sQuery(id+"F0.wireOp",EDGE,"E141.MirrorCS"),sQuery(id+"F0.wireOp",EDGE,"E142.MirrorCS"),sQuery(id+"F0.wireOp",EDGE,"E143.MirrorCS"),sQuery(id+"F0.wireOp",EDGE,"E144.MirrorCS"),sQuery(id+"F0.wireOp",EDGE,"E145.MirrorCS"),sQuery(id+"F0.wireOp",EDGE,"E146.MirrorCS"),sQuery(id+"F0.wireOp",EDGE,"E147.MirrorCS"),sQuery(id+"F0.wireOp",EDGE,"E148.MirrorCS"),sQuery(id+"F0.wireOp",EDGE,"E149.MirrorCS"),sQuery(id+"F0.wireOp",EDGE,"E150.MirrorCS"),sQuery(id+"F0.wireOp",EDGE,"E151.MirrorCS"),sQuery(id+"F0.wireOp",EDGE,"E152.MirrorCS"),sQuery(id+"F0.wireOp",EDGE,"E153.MirrorCS"),sQuery(id+"F0.wireOp",EDGE,"E154.MirrorCS"),sQuery(id+"F0.wireOp",EDGE,"E155.MirrorCS"),sQuery(id+"F0.wireOp",EDGE,"E156.MirrorCS"),sQuery(id+"F0.wireOp",EDGE,"E157.MirrorCS"),sQuery(id+"F0.wireOp",EDGE,"E158.MirrorCS"),sQuery(id+"F0.wireOp",EDGE,"E159"),sQuery(id+"F0.wireOp",EDGE,"E160"),sQuery(id+"F0.wireOp",EDGE,"E161"),sQuery(id+"F0.wireOp",EDGE,"E162"),sQuery(id+"F0.wireOp",EDGE,"E163"),sQuery(id+"F0.wireOp",EDGE,"E164"),sQuery(id+"F0.wireOp",EDGE,"E165"),sQuery(id+"F0.wireOp",EDGE,"E166"),sQuery(id+"F0.wireOp",EDGE,"E167"),sQuery(id+"F0.wireOp",EDGE,"E168"),sQuery(id+"F0.wireOp",EDGE,"E169"),sQuery(id+"F0.wireOp",EDGE,"E170"),sQuery(id+"F0.wireOp",EDGE,"E171"),sQuery(id+"F0.wireOp",EDGE,"E172"),sQuery(id+"F0.wireOp",EDGE,"E173"),sQuery(id+"F0.wireOp",EDGE,"E174"),sQuery(id+"F0.wireOp",EDGE,"E175"),sQuery(id+"F0.wireOp",EDGE,"E176"),sQuery(id+"F0.wireOp",EDGE,"E177"),sQuery(id+"F0.wireOp",EDGE,"E178"),sQuery(id+"F0.wireOp",EDGE,"E179.0"),sQuery(id+"F0.wireOp",EDGE,"E180"),sQuery(id+"F0.wireOp",EDGE,"E181"),sQuery(id+"F0.wireOp",EDGE,"E182"),sQuery(id+"F0.wireOp",EDGE,"E183"),sQuery(id+"F0.wireOp",EDGE,"E184"),sQuery(id+"F0.wireOp",EDGE,"E185"),sQuery(id+"F0.wireOp",EDGE,"E186"),sQuery(id+"F0.wireOp",EDGE,"E187"),sQuery(id+"F0.wireOp",EDGE,"E188"),sQuery(id+"F0.wireOp",EDGE,"E189"),sQuery(id+"F0.wireOp",EDGE,"E190"),sQuery(id+"F0.wireOp",EDGE,"E191"),sQuery(id+"F0.wireOp",EDGE,"E192"),sQuery(id+"F0.wireOp",EDGE,"E193"),sQuery(id+"F0.wireOp",EDGE,"E194.0"),sQuery(id+"F0.wireOp",EDGE,"E195"),sQuery(id+"F0.wireOp",EDGE,"E196.0"),sQuery(id+"F0.wireOp",EDGE,"E198.0"),sQuery(id+"F0.wireOp",EDGE,"E199.0"),sQuery(id+"F0.wireOp",EDGE,"E200"),sQuery(id+"F0.wireOp",EDGE,"E201")])],"isStart":false});
            var sketch = newSketch(context, id + "F2", { "sketchPlane" : qUnion([Q0])});
            skLineSegment(sketch, "E202.bottom", {"start": v(-75, 175) * mm, "end": v(-70, 175) * mm});
            skLineSegment(sketch, "E202.top", {"start": v(-75, 195) * mm, "end": v(-70, 195) * mm});
            skLineSegment(sketch, "E202.left", {"start": v(-75, 175) * mm, "end": v(-75, 195) * mm});
            skLineSegment(sketch, "E202.right", {"start": v(-70, 175) * mm, "end": v(-70, 195) * mm});
            skLineSegment(sketch, "E203.bottom", {"start": v(320, 295) * mm, "end": v(330, 295) * mm});
            skLineSegment(sketch, "E203.top", {"start": v(320, 355) * mm, "end": v(330, 355) * mm});
            skLineSegment(sketch, "E203.left", {"start": v(320, 295) * mm, "end": v(320, 355) * mm});
            skLineSegment(sketch, "E203.right", {"start": v(330, 295) * mm, "end": v(330, 355) * mm});
            skLineSegment(sketch, "E204.bottom", {"start": v(725, 475) * mm, "end": v(720, 475) * mm});
            skLineSegment(sketch, "E204.top", {"start": v(725, 455) * mm, "end": v(720, 455) * mm});
            skLineSegment(sketch, "E204.left", {"start": v(725, 475) * mm, "end": v(725, 455) * mm});
            skLineSegment(sketch, "E204.right", {"start": v(720, 475) * mm, "end": v(720, 455) * mm});
            skLineSegment(sketch, "E205.bottom", {"start": v(-113.03, 745) * mm, "end": v(-93.03, 745) * mm});
            skLineSegment(sketch, "E205.top", {"start": v(-113.03, 740) * mm, "end": v(-93.03, 740) * mm});
            skLineSegment(sketch, "E205.left", {"start": v(-113.03, 745) * mm, "end": v(-113.03, 740) * mm});
            skLineSegment(sketch, "E205.right", {"start": v(-93.03, 745) * mm, "end": v(-93.03, 740) * mm});
            skLineSegment(sketch, "E206.bottom", {"start": v(763.03, -95) * mm, "end": v(743.03, -95) * mm});
            skLineSegment(sketch, "E206.top", {"start": v(763.03, -90) * mm, "end": v(743.03, -90) * mm});
            skLineSegment(sketch, "E206.left", {"start": v(763.03, -95) * mm, "end": v(763.03, -90) * mm});
            skLineSegment(sketch, "E206.right", {"start": v(743.03, -95) * mm, "end": v(743.03, -90) * mm});
            skSolve(sketch);
        }
        {
            var Q0;
            Q0 = qSketchRegion(id + "F2", true);
            extrude(context, id + "F3", {"entities" : qUnion([Q0]), "operationType" : NewBodyOperationType.ADD, "depth" : 25 * mm, "offsetDistance" : 25 * mm});
        }
        {
            var Q0;
            Q0=makeQuery(id+"F3.opExtrude","CAP_FACE",FACE,{"disambiguationData":[OSD([sQuery(id+"F2.wireOp",EDGE,"E202.bottom"),sQuery(id+"F2.wireOp",EDGE,"E202.top"),sQuery(id+"F2.wireOp",EDGE,"E202.left"),sQuery(id+"F2.wireOp",EDGE,"E202.right")])],"isStart":false});
            var sketch = newSketch(context, id + "F4", { "sketchPlane" : qUnion([Q0])});
            skLineSegment(sketch, "E207.bottom", {"start": v(-70, 175) * mm, "end": v(-113.03, 175) * mm});
            skLineSegment(sketch, "E207.top", {"start": v(-70, 745) * mm, "end": v(-113.03, 745) * mm});
            skLineSegment(sketch, "E207.left", {"start": v(-70, 175) * mm, "end": v(-70, 745) * mm});
            skLineSegment(sketch, "E207.right", {"start": v(-113.03, 175) * mm, "end": v(-113.03, 745) * mm});
            skLineSegment(sketch, "E208.bottom", {"start": v(720, 475) * mm, "end": v(763.03, 475) * mm});
            skLineSegment(sketch, "E208.top", {"start": v(720, -95) * mm, "end": v(763.03, -95) * mm});
            skLineSegment(sketch, "E208.left", {"start": v(720, 475) * mm, "end": v(720, -95) * mm});
            skLineSegment(sketch, "E208.right", {"start": v(763.03, 475) * mm, "end": v(763.03, -95) * mm});
            skSolve(sketch);
        }
        {
            var Q0;
            {var subQ2=sQuery(id+"F4.wireOp",EDGE,"E207.top");Q0=makeQuery(id+"F4.imprint","IMPRINT",FACE,{"disambiguationData":[TD([[makeQuery(id+"F4.imprint","IMPRINT",EDGE,{"derivedFrom":subQ2}),1.0]])]});}
            var Q1;
            Q1=makeQuery(id+"F4.imprint","IMPRINT",FACE,{"disambiguationData":[TD([[makeQuery(id+"F4.imprint","IMPRINT",EDGE,{"derivedFrom":sQuery(id+"F4.wireOp",EDGE,"E208.bottom")}),-1.0]])]});
            extrude(context, id + "F5", {"entities" : qUnion([Q0, Q1]), "operationType" : NewBodyOperationType.ADD, "oppositeDirection" : true, "depth" : 5 * mm, "offsetDistance" : 25 * mm});
        }
        {
            var Q0;
            Q0=makeQuery(id+"F3.opExtrude","CAP_FACE",FACE,{"disambiguationData":[OSD([sQuery(id+"F2.wireOp",EDGE,"E203.bottom"),sQuery(id+"F2.wireOp",EDGE,"E203.top"),sQuery(id+"F2.wireOp",EDGE,"E203.left"),sQuery(id+"F2.wireOp",EDGE,"E203.right")])],"isStart":false});
            var sketch = newSketch(context, id + "F6", { "sketchPlane" : qUnion([Q0])});
            skLineSegment(sketch, "E209.bottom", {"start": v(320, 295) * mm, "end": v(763.03, 295) * mm});
            skLineSegment(sketch, "E209.top", {"start": v(320, 355) * mm, "end": v(763.03, 355) * mm});
            skLineSegment(sketch, "E209.left", {"start": v(320, 295) * mm, "end": v(320, 355) * mm});
            skLineSegment(sketch, "E209.right", {"start": v(763.03, 295) * mm, "end": v(763.03, 355) * mm});
            skLineSegment(sketch, "E210.bottom", {"start": v(330, 295) * mm, "end": v(-113.03, 295) * mm});
            skLineSegment(sketch, "E210.top", {"start": v(330, 355) * mm, "end": v(-113.03, 355) * mm});
            skLineSegment(sketch, "E210.left", {"start": v(330, 295) * mm, "end": v(330, 355) * mm});
            skLineSegment(sketch, "E210.right", {"start": v(-113.03, 295) * mm, "end": v(-113.03, 355) * mm});
            skSolve(sketch);
        }
        {
            var Q0;
            Q0 = qSketchRegion(id + "F6", true);
            extrude(context, id + "F7", {"entities" : qUnion([Q0]), "operationType" : NewBodyOperationType.ADD, "oppositeDirection" : true, "depth" : 5 * mm, "offsetDistance" : 25 * mm});
        }
        {
            var Q0;
            Q0=makeQuery(id+"F7.boolean.opBoolean","MERGE",FACE,{"derivedFrom":[makeQuery(id+"F3.boolean.opBoolean","MERGE",FACE,{"derivedFrom":[makeQuery(id+"F1.opExtrude","SWEPT_FACE",FACE,{"disambiguationData":[OSD([sQuery(id+"F0.wireOp",EDGE,"E17.3"),sQuery(id+"F0.wireOp",EDGE,"E201")])]}),makeQuery(id+"F3.opExtrude","SWEPT_FACE",FACE,{"disambiguationData":[OSD([sQuery(id+"F2.wireOp",EDGE,"E203.bottom")])]})]}),makeQuery(id+"F7.opExtrude","SWEPT_FACE",FACE,{"disambiguationData":[OSD([sQuery(id+"F6.wireOp",EDGE,"E209.bottom"),sQuery(id+"F6.wireOp",EDGE,"E210.bottom")])]})]});
            var sketch = newSketch(context, id + "F8", { "sketchPlane" : qUnion([Q0])});
            skLineSegment(sketch, "E211.bottom", {"start": v(320, 50) * mm, "end": v(330, 50) * mm});
            skLineSegment(sketch, "E211.top", {"start": v(320, 30) * mm, "end": v(330, 30) * mm});
            skLineSegment(sketch, "E211.left", {"start": v(320, 50) * mm, "end": v(320, 30) * mm});
            skLineSegment(sketch, "E211.right", {"start": v(330, 50) * mm, "end": v(330, 30) * mm});
            skSolve(sketch);
        }
        {
            var Q0;
            Q0=makeQuery(id+"F8.imprint","IMPRINT",FACE,{"disambiguationData":[TD([[makeQuery(id+"F8.imprint","IMPRINT",EDGE,{"derivedFrom":sQuery(id+"F8.wireOp",EDGE,"E211.bottom")}),-1.0]])]});
            extrude(context, id + "F9", {"entities" : qUnion([Q0]), "operationType" : NewBodyOperationType.REMOVE, "oppositeDirection" : true, "depth" : 60 * mm, "offsetDistance" : 25 * mm});
        }
    });
